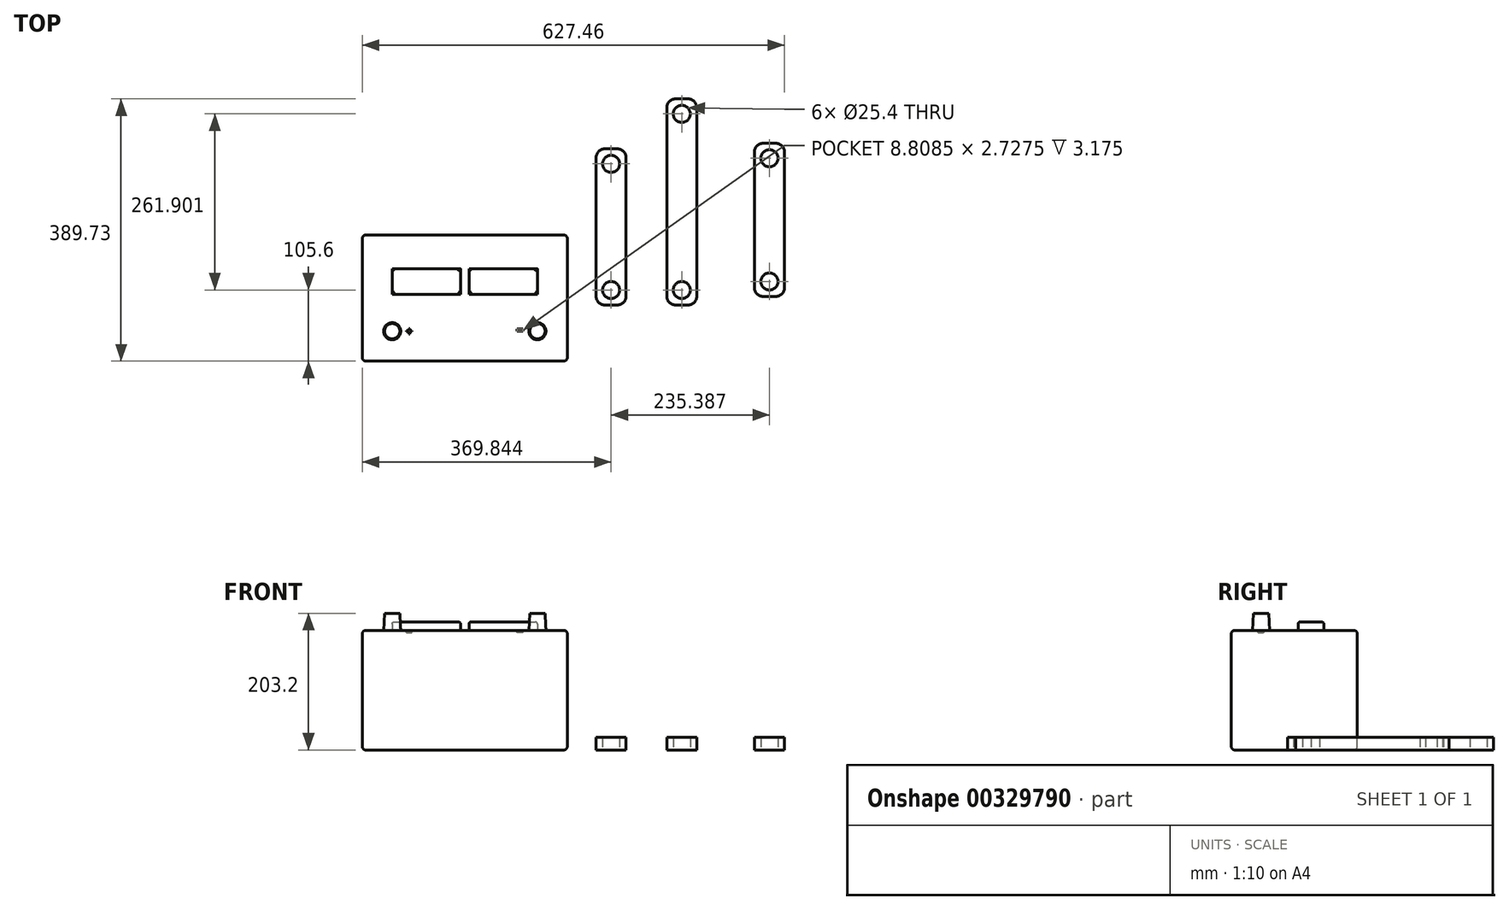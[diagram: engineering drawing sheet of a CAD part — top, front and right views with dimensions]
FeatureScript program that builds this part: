
annotation { "Feature Type Name" : "Feature", "Feature Type Description" : "" }
export const myFeature = defineFeature(function(context is Context, id is Id, definition is map)
    precondition{}
    {
        {
            var Q0;
            Q0=qCreatedBy(makeId("Front.planeOp"),FACE);
            var sketch = newSketch(context, id + "F0", { "sketchPlane" : qUnion([Q0])});
            skLineSegment(sketch, "E0.bottom", {"start": v(0, 0) * mm, "end": v(-304.8, 0) * mm});
            skLineSegment(sketch, "E0.top", {"start": v(0, 177.8) * mm, "end": v(-304.8, 177.8) * mm});
            skLineSegment(sketch, "E0.left", {"start": v(0, 0) * mm, "end": v(0, 177.8) * mm});
            skLineSegment(sketch, "E0.right", {"start": v(-304.8, 0) * mm, "end": v(-304.8, 177.8) * mm});
            skSolve(sketch);
        }
        {
            var Q0;
            Q0=qSketchRegion(id+"F0",true);
            extrude(context, id + "F1", {"entities" : qUnion([Q0]), "depth" : 187.32 * mm});
        }
        {
            var Q0;
            Q0=makeQuery(id+"F1.opExtrude","CAP_FACE",FACE,{"disambiguationData":[OSD([sQuery(id+"F0.wireOp",EDGE,"E0.bottom"),sQuery(id+"F0.wireOp",EDGE,"E0.top"),sQuery(id+"F0.wireOp",EDGE,"E0.left"),sQuery(id+"F0.wireOp",EDGE,"E0.right")])],"isStart":false});
            var Q1;
            Q1=makeQuery(id+"F1.opExtrude","SWEPT_FACE",FACE,{"disambiguationData":[OSD([sQuery(id+"F0.wireOp",EDGE,"E0.top")])]});
            var Q2;
            Q2=makeQuery(id+"F1.opExtrude","CAP_FACE",FACE,{"disambiguationData":[OSD([sQuery(id+"F0.wireOp",EDGE,"E0.bottom"),sQuery(id+"F0.wireOp",EDGE,"E0.top"),sQuery(id+"F0.wireOp",EDGE,"E0.left"),sQuery(id+"F0.wireOp",EDGE,"E0.right")])],"isStart":true});
            var Q3;
            Q3=makeQuery(id+"F1.opExtrude","SWEPT_FACE",FACE,{"disambiguationData":[OSD([sQuery(id+"F0.wireOp",EDGE,"E0.bottom")])]});
            fillet(context, id + "F2", {"entities" : qUnion([Q0, Q1, Q2, Q3]), "radius" : 5.08 * mm, "tangentPropagation" : true, "allowEdgeOverflow" : false});
        }
        {
            var Q0;
            Q0=makeQuery(id+"F1.opExtrude","SWEPT_FACE",FACE,{"disambiguationData":[OSD([sQuery(id+"F0.wireOp",EDGE,"E0.top")])]});
            var sketch = newSketch(context, id + "F3", { "sketchPlane" : qUnion([Q0])});
            skCircle(sketch, "E1", {"center": v(-260.35, -142.88) * mm, "radius": 12.7 * mm});
            skCircle(sketch, "E2", {"center": v(-44.45, -142.88) * mm, "radius": 12.7 * mm});
            skLineSegment(sketch, "E3.bottom", {"start": v(-260.35, -87.98) * mm, "end": v(-158.75, -87.98) * mm});
            skLineSegment(sketch, "E3.top", {"start": v(-260.35, -49.88) * mm, "end": v(-158.75, -49.88) * mm});
            skLineSegment(sketch, "E3.left", {"start": v(-260.35, -87.98) * mm, "end": v(-260.35, -49.88) * mm});
            skLineSegment(sketch, "E3.right", {"start": v(-158.75, -87.98) * mm, "end": v(-158.75, -49.88) * mm});
            skLineSegment(sketch, "E4.bottom", {"start": v(-146.05, -87.98) * mm, "end": v(-44.45, -87.98) * mm});
            skLineSegment(sketch, "E4.top", {"start": v(-146.05, -49.88) * mm, "end": v(-44.45, -49.88) * mm});
            skLineSegment(sketch, "E4.left", {"start": v(-146.05, -87.98) * mm, "end": v(-146.05, -49.88) * mm});
            skLineSegment(sketch, "E4.right", {"start": v(-44.45, -87.98) * mm, "end": v(-44.45, -49.88) * mm});
            skText(sketch, "E5", { "text": "+", "fontName": "OpenSans-Regular.ttf"});
            skText(sketch, "E6", { "text": "-", "fontName": "OpenSans-Regular.ttf"});
            const initialGuessF3  = {"E5": [-0.2401, -0.14923, 1, 0, 0.0127], "E6": [-0.0762, -0.15113, 1, 0, 0.02646]};
            skSetInitialGuess(sketch, initialGuessF3);
            skSolve(sketch);
        }
        {
            var Q0;
            Q0=makeQuery(id+"F3.imprint","IMPRINT",FACE,{"disambiguationData":[TD([[makeQuery(id+"F3.imprint","IMPRINT",EDGE,{"derivedFrom":sQuery(id+"F3.wireOp",EDGE,"E3.bottom")}),1.0]])]});
            var Q1;
            Q1=makeQuery(id+"F3.imprint","IMPRINT",FACE,{"disambiguationData":[TD([[makeQuery(id+"F3.imprint","IMPRINT",EDGE,{"derivedFrom":sQuery(id+"F3.wireOp",EDGE,"E4.bottom")}),1.0]])]});
            extrude(context, id + "F4", {"entities" : qUnion([Q0, Q1]), "operationType" : NewBodyOperationType.ADD, "depth" : 12.7 * mm});
        }
        {
            var Q0;
            Q0=makeQuery(id+"F3.imprint","IMPRINT",FACE,{"disambiguationData":[TD([[makeQuery(id+"F3.imprint","IMPRINT",EDGE,{"derivedFrom":sQuery(id+"F3.wireOp",EDGE,"E1")}),1.0]])]});
            var Q1;
            Q1=makeQuery(id+"F3.imprint","IMPRINT",FACE,{"disambiguationData":[TD([[makeQuery(id+"F3.imprint","IMPRINT",EDGE,{"derivedFrom":sQuery(id+"F3.wireOp",EDGE,"E2")}),1.0]])]});
            extrude(context, id + "F5", {"entities" : qUnion([Q0, Q1]), "operationType" : NewBodyOperationType.ADD, "depth" : 25.4 * mm, "hasDraft" : true, "draftAngle" : 3 * degree, "draftPullDirection" : true});
        }
        {
            var Q0;
            Q0=makeQuery(id+"F4.opExtrude","CAP_FACE",FACE,{"disambiguationData":[OSD([sQuery(id+"F3.wireOp",EDGE,"E3.bottom"),sQuery(id+"F3.wireOp",EDGE,"E3.top"),sQuery(id+"F3.wireOp",EDGE,"E3.left"),sQuery(id+"F3.wireOp",EDGE,"E3.right")])],"isStart":false});
            var Q1;
            Q1=makeQuery(id+"F4.opExtrude","CAP_FACE",FACE,{"disambiguationData":[OSD([sQuery(id+"F3.wireOp",EDGE,"E4.bottom"),sQuery(id+"F3.wireOp",EDGE,"E4.top"),sQuery(id+"F3.wireOp",EDGE,"E4.left"),sQuery(id+"F3.wireOp",EDGE,"E4.right")])],"isStart":false});
            fillet(context, id + "F6", {"entities" : qUnion([Q0, Q1]), "radius" : 3.17 * mm, "tangentPropagation" : true, "allowEdgeOverflow" : false});
        }
        {
            var Q0;
            Q0=makeQuery(id+"F3.imprint","IMPRINT",FACE,{"disambiguationData":[TD([[makeQuery(id+"F3.imprint","IMPRINT",EDGE,{"derivedFrom":sQuery(id+"F3.wireOp",EDGE,"E5.sketch_text.stroke-0")}),-1.0]])]});
            var Q1;
            Q1=makeQuery(id+"F3.imprint","IMPRINT",FACE,{"disambiguationData":[TD([[makeQuery(id+"F3.imprint","IMPRINT",EDGE,{"derivedFrom":sQuery(id+"F3.wireOp",EDGE,"E6.sketch_text.stroke-0")}),-1.0]])]});
            extrude(context, id + "F7", {"entities" : qUnion([Q0, Q1]), "operationType" : NewBodyOperationType.REMOVE, "oppositeDirection" : true, "depth" : 3.17 * mm});
        }
        {
            var Q0;
            Q0=qCreatedBy(makeId("Top.planeOp"),FACE);
            var sketch = newSketch(context, id + "F8", { "sketchPlane" : qUnion([Q0])});
            skLineSegment(sketch, "E7.bottom", {"start": v(55.52, 128.1) * mm, "end": v(74.57, 128.1) * mm});
            skLineSegment(sketch, "E7.top", {"start": v(55.52, -103.95) * mm, "end": v(74.57, -103.95) * mm});
            skLineSegment(sketch, "E7.left", {"start": v(42.82, 115.4) * mm, "end": v(42.82, -91.25) * mm});
            skLineSegment(sketch, "E7.right", {"start": v(87.27, 115.4) * mm, "end": v(87.27, -91.25) * mm});
            skCircle(sketch, "E8", {"center": v(65.04, 105.88) * mm, "radius": 12.7 * mm});
            skCircle(sketch, "E9", {"center": v(65.04, -81.73) * mm, "radius": 12.7 * mm});
            skPoint(sketch, "E10.visualSharp", {"position": v(87.27, 128.1) * mm});
            skArc(sketch, "E10.filletArc", {"start": v(87.27, 115.4) * mm, "mid": v(83.55, 124.38) * mm, "end": v(74.57, 128.1) * mm});
            skPoint(sketch, "E11.visualSharp", {"position": v(42.82, -103.95) * mm});
            skArc(sketch, "E11.filletArc", {"start": v(42.82, -91.25) * mm, "mid": v(46.54, -100.23) * mm, "end": v(55.52, -103.95) * mm});
            skPoint(sketch, "E12.visualSharp", {"position": v(87.27, -103.95) * mm});
            skArc(sketch, "E12.filletArc", {"start": v(74.57, -103.95) * mm, "mid": v(83.55, -100.23) * mm, "end": v(87.27, -91.25) * mm});
            skPoint(sketch, "E13.visualSharp", {"position": v(42.82, 128.1) * mm});
            skArc(sketch, "E13.filletArc", {"start": v(55.52, 128.1) * mm, "mid": v(46.54, 124.38) * mm, "end": v(42.82, 115.4) * mm});
            skLineSegment(sketch, "E14.bottom", {"start": v(160.66, 202.4) * mm, "end": v(179.7, 202.4) * mm});
            skLineSegment(sketch, "E14.top", {"start": v(160.66, -103.95) * mm, "end": v(179.7, -103.95) * mm});
            skLineSegment(sketch, "E14.left", {"start": v(147.96, 189.7) * mm, "end": v(147.96, -91.25) * mm});
            skLineSegment(sketch, "E14.right", {"start": v(192.4, 189.7) * mm, "end": v(192.4, -91.25) * mm});
            skCircle(sketch, "E15", {"center": v(170.18, 180.17) * mm, "radius": 12.7 * mm});
            skCircle(sketch, "E16", {"center": v(170.18, -81.73) * mm, "radius": 12.7 * mm});
            skPoint(sketch, "E17.visualSharp", {"position": v(192.4, 202.4) * mm});
            skArc(sketch, "E17.filletArc", {"start": v(192.4, 189.7) * mm, "mid": v(188.69, 198.68) * mm, "end": v(179.7, 202.4) * mm});
            skPoint(sketch, "E18.visualSharp", {"position": v(147.96, -103.95) * mm});
            skArc(sketch, "E18.filletArc", {"start": v(147.96, -91.25) * mm, "mid": v(151.68, -100.23) * mm, "end": v(160.66, -103.95) * mm});
            skPoint(sketch, "E19.visualSharp", {"position": v(192.4, -103.95) * mm});
            skArc(sketch, "E19.filletArc", {"start": v(179.7, -103.95) * mm, "mid": v(188.69, -100.23) * mm, "end": v(192.4, -91.25) * mm});
            skPoint(sketch, "E20.visualSharp", {"position": v(147.96, 202.4) * mm});
            skArc(sketch, "E20.filletArc", {"start": v(160.66, 202.4) * mm, "mid": v(151.68, 198.68) * mm, "end": v(147.96, 189.7) * mm});
            skLineSegment(sketch, "E21.bottom", {"start": v(290.9, 136.53) * mm, "end": v(309.96, 136.53) * mm});
            skLineSegment(sketch, "E21.top", {"start": v(290.9, -91.25) * mm, "end": v(309.96, -91.25) * mm});
            skLineSegment(sketch, "E21.left", {"start": v(278.2, 123.83) * mm, "end": v(278.2, -78.55) * mm});
            skLineSegment(sketch, "E21.right", {"start": v(322.66, 123.83) * mm, "end": v(322.66, -78.55) * mm});
            skCircle(sketch, "E22", {"center": v(300.43, 114.3) * mm, "radius": 12.7 * mm});
            skCircle(sketch, "E23", {"center": v(300.43, -69.03) * mm, "radius": 12.7 * mm});
            skPoint(sketch, "E24.visualSharp", {"position": v(322.66, 136.53) * mm});
            skArc(sketch, "E24.filletArc", {"start": v(322.66, 123.83) * mm, "mid": v(318.94, 132.81) * mm, "end": v(309.96, 136.53) * mm});
            skPoint(sketch, "E25.visualSharp", {"position": v(278.2, -91.25) * mm});
            skArc(sketch, "E25.filletArc", {"start": v(278.2, -78.55) * mm, "mid": v(281.93, -87.53) * mm, "end": v(290.9, -91.25) * mm});
            skPoint(sketch, "E26.visualSharp", {"position": v(322.66, -91.25) * mm});
            skArc(sketch, "E26.filletArc", {"start": v(309.96, -91.25) * mm, "mid": v(318.94, -87.53) * mm, "end": v(322.66, -78.55) * mm});
            skPoint(sketch, "E27.visualSharp", {"position": v(278.2, 136.53) * mm});
            skArc(sketch, "E27.filletArc", {"start": v(290.9, 136.53) * mm, "mid": v(281.93, 132.81) * mm, "end": v(278.2, 123.83) * mm});
            skSolve(sketch);
        }
        {
            var Q0;
            Q0=makeQuery(id+"F8.imprint","IMPRINT",FACE,{"disambiguationData":[TD([[makeQuery(id+"F8.imprint","IMPRINT",EDGE,{"derivedFrom":sQuery(id+"F8.wireOp",EDGE,"E7.bottom")}),-1.0]])]});
            var Q1;
            Q1=makeQuery(id+"F8.imprint","IMPRINT",FACE,{"disambiguationData":[TD([[makeQuery(id+"F8.imprint","IMPRINT",EDGE,{"derivedFrom":sQuery(id+"F8.wireOp",EDGE,"E14.bottom")}),-1.0]])]});
            var Q2;
            Q2=makeQuery(id+"F8.imprint","IMPRINT",FACE,{"disambiguationData":[TD([[makeQuery(id+"F8.imprint","IMPRINT",EDGE,{"derivedFrom":sQuery(id+"F8.wireOp",EDGE,"E21.bottom")}),-1.0]])]});
            extrude(context, id + "F9", {"entities" : qUnion([Q0, Q1, Q2]), "depth" : 19.05 * mm});
        }
    });
